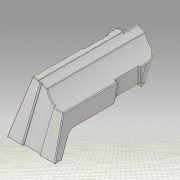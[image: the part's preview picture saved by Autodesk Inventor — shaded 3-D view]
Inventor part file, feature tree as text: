
AUTODESK INVENTOR PART (.ipt)
format: ipt  version: 2018 (Build 220112000, 112)  size: 1,081,856 bytes
history: native  units: in
note: dims shown in document units (in); Inventor stores cm internally (conversion verified against a paired STEP export)
features: sketch x36, extrude x33, fillet x12, plane x9, projected_geometry x8, mirror x3
ambient origin geometry x8: Origin, YZ Plane, XZ Plane, XY Plane, X Axis, Y Axis, Z Axis, Center Point
bodies: Solid1 (feature_tree)
feature tree (101):
  extrude  "Extrusion1"  Depth=1.203in
  sketch  "Sketch2"  dims[d2=0.336in d3=0.0in d4=0.4673in]
  plane  "Work Plane2"
  plane  "Work Plane1"
  sketch  "Sketch7"  dims[d5=0.7696in d18=0.183in]
  extrude  "Extrusion6"  Depth=0.4673in
  extrude  "Extrusion7"  Depth=0.183in
  extrude  "Extrusion8"  Depth=0.655in
  extrude  "Extrusion9"  Depth=0.77in TaperAngle=0.0deg
  extrude  "Extrusion10"  Depth=0.635in TaperAngle=0.0deg
  extrude  "Extrusion11"  Depth=0.635in TaperAngle=0.0deg
  extrude  "Extrusion12"  Depth=0.085in
  extrude  "Extrusion13"  Depth=0.635in TaperAngle=0.0deg
  extrude  "Extrusion14"  Depth=0.391in
  plane  "Work Plane3"
  mirror  "Mirror1"
  extrude  "Extrusion15"  Depth=1.0in TaperAngle=0.0deg
  extrude  "Extrusion16"  Depth=1.0in TaperAngle=0.0deg
  extrude  "Extrusion17"  TaperAngle=90.0deg  [1 undecoded]
  plane  "Work Plane4"
  extrude  "Extrusion18"  Depth=0.04in
  fillet  "Fillet1"  Radius=0.105in
  sketch  "Sketch25"  dims[d57=3.0in d58=0.0in d59=0.04in]
  sketch  "Sketch26"  dims[d66=0.172in d67=0.4in d68=0.0in d69=0.041in]
  extrude  "Extrusion20"  Depth=0.25in
  extrude  "Extrusion21"  Depth=0.04in
  plane  "Work Plane5"
  extrude  "Extrusion26"  Depth=0.4in TaperAngle=0.0deg
  fillet  "Fillet3"  Radius=0.041in
  plane  "Work Plane6"
  extrude  "Extrusion29"  TaperAngle=90.0deg  [1 undecoded]
  extrude  "Extrusion30"  Depth=0.2in
  extrude  "Extrusion31"  Depth=2.0in TaperAngle=0.0deg
  plane  "Work Plane7"
  extrude  "Extrusion32"  [1 undecoded]
  extrude  "Extrusion33"  Depth=2.0in TaperAngle=0.0deg
  extrude  "Extrusion34"  Depth=2.0in TaperAngle=0.0deg
  sketch  "Sketch43"  dims[d115=0.125in d116=2.0in d117=0.0in]
  extrude  "Extrusion35"  Depth=2.0in TaperAngle=0.0deg
  mirror  "Mirror5"
  extrude  "Extrusion36"  Depth=2.0in TaperAngle=0.0deg
  fillet  "Fillet4"  Radius=0.041in
  extrude  "Extrusion37"  Depth=2.0in TaperAngle=0.0deg
  sketch  "Sketch47"  dims[d132=0.17in d133=90.0deg d134=0.115in d135=0.07in d136=0.0in]
  plane  "Work Plane9"
  extrude  "Extrusion38"  Depth=1.0808in
  extrude  "Extrusion39"  Depth=2.0in TaperAngle=0.0deg
  fillet  "Fillet5"  Radius=2.0in
  fillet  "Fillet7"  Radius=0.1in
  fillet  "Fillet8"  Radius=0.176in
  fillet  "Fillet9"  Radius=0.176in
  extrude  "Extrusion40"  Depth=0.08in
  fillet  "Fillet10"  [1 undecoded]
  extrude  "Extrusion41"  Depth=0.115in TaperAngle=90.0deg
  fillet  "Fillet11"  Radius=0.07in
  extrude  "Extrusion42"  Depth=0.01in
  mirror  "Mirror6"
  fillet  "Fillet12"  Radius=0.01in
  fillet  "Fillet13"  Radius=0.01in
  extrude  "Extrusion44"  Depth=0.01in
  extrude  "Extrusion45"  Depth=0.01in
  fillet  "Fillet14"  Radius=0.041in
  sketch  "Sketch1"  dims[d0=0.424in d1=1.203in]
  sketch  "Sketch8"  dims[d20=0.636in d21=0.655in]
  sketch  "Sketch11"  dims[d22=0.311in d23=0.77in d24=0.0in]
  sketch  "Sketch12"  dims[d25=0.635in d26=0.0in d27=0.635in d28=0.0in]
  sketch  "Sketch13"  dims[d29=0.635in d30=0.0in d31=0.635in d32=0.0in]
  sketch  "Sketch14"  dims[d33=0.635in d34=0.0in d35=0.085in]
  projected_geometry  "Projected Loop1"
  sketch  "Sketch16"  dims[d36=0.122in d37=0.635in d38=0.0in]
  sketch  "Sketch18"  dims[d39=0.175in d40=0.391in]
  sketch  "Sketch19"  dims[d41=0.635in d42=0.0in d43=1.0in d44=0.0in]
  sketch  "Sketch20"  dims[d45=1.0in d46=0.0in d47=1.0in d48=0.0in]
  projected_geometry  "Projected Loop2"
  sketch  "Sketch21"  dims[d49=1.0in d50=0.0in d51=90.0deg]
  sketch  "Sketch22"  dims[d52=0.08in d53=0.04in d54=0.105in]
  projected_geometry  "Projected Loop3"
  sketch  "Sketch23"  dims[d55=0.1in d56=0.25in]
  sketch  "Sketch27"  dims[d70=0.4in d71=0.0in d81=90.0deg]
  sketch  "Sketch32"  dims[d86=0.1in d87=0.2in]
  sketch  "Sketch36"  dims[d88=0.015in d89=2.0in d90=0.0in]
  sketch  "Sketch37"  dims[d91=0.014in d94=-0.137in]
  sketch  "Sketch39"  dims[d101=0.636in d102=2.0in d103=0.0in]
  projected_geometry  "Projected Loop7"
  sketch  "Sketch40"  dims[d104=2.0in d105=0.0in d106=2.0in d107=0.0in]
  projected_geometry  "Projected Loop8"
  sketch  "Sketch41"  dims[d108=90.0deg d109=2.0in d110=0.0in]
  sketch  "Sketch42"  dims[d111=1.16in d112=2.0in d113=0.0in d114=0.041in]
  sketch  "Sketch44"  dims[d118=0.25in d119=1.0808in]
  sketch  "Sketch45"  dims[d120=0.25in d121=2.0in d122=0.0in d123=2.0in d124=0.0in d125=0.1in d126=0.176in d127=0.176in]
  projected_geometry  "Projected Loop9"
  sketch  "Sketch46"  dims[d128=0.087in d129=0.0in d130=0.08in d131=0.0in]
  plane  "Work Plane8"
  sketch  "Sketch48"  dims[d137=1.0in d138=0.0in d139=0.18in d141=0.01in d142=0.01in]
  sketch  "Sketch49"  dims[d143=0.01in d144=0.075in]
  sketch  "Sketch50"  dims[d145=1.1in d146=0.0in d147=0.01in d148=0.041in]
  projected_geometry  "Projected Loop10"
  sketch  "Sketch51"  dims[d149=0.02in d150=0.0in]
  sketch  "Sketch53"  dims[d151=0.01in]
  projected_geometry  "Projected Loop12"
  sketch  "Sketch54"  dims[d152=0.025in d153=1.0in d154=0.0in d157=0.021in d158=0.015in d159=0.02in d160=0.0in d162=0.02in d163=0.0in d164=0.01in]
note: 4 required parameter values undecoded (feature->parameter linkage not recoverable at this tier; creation-order binding heuristic only, values carry confidence <= 0.55)
